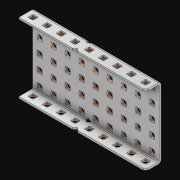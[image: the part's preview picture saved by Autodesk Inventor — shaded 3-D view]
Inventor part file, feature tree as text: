
AUTODESK INVENTOR PART (.ipt)
format: ipt  version: 2021 (Build 250183000, 183)  size: 3,008,512 bytes
history: native  units: in
note: dims shown in document units (in); Inventor stores cm internally (conversion verified against a paired STEP export)
features: extrude x64, other x63, sketch x4, thicken_offset x3, pattern_linear x3, imported_body x1
ambient origin geometry x8: Origin, YZ Plane, XZ Plane, XY Plane, X Axis, Y Axis, Z Axis, Center Point
bodies: Solid1 (feature_tree)
feature tree (138):
  thicken_offset  "Thicken1"
  thicken_offset  "Thicken2"
  thicken_offset  "Thicken3"
  pattern_linear  "Rectangular Pattern1"  Spacing1=0.001in  [1 undecoded]
  pattern_linear  "Rectangular Pattern2"  Spacing1=0.001in  [1 undecoded]
  pattern_linear  "Rectangular Pattern3"  Spacing1=0.182in  [1 undecoded]
  extrude  "Extrusion1"  Depth=0.063in TaperAngle=0.0deg
  sketch  "Sketch1"  dims[d0=0.001in]
  other  "Srf1"
  sketch  "Sketch2"  dims[d1=0.001in]
  other  "Srf2"
  sketch  "Sketch3"  dims[d2=0.001in]
  other  "Srf3"
  other  "Srf4"
  other  "Srf5"
  other  "Srf6"
  other  "Srf7"
  other  "Srf8"
  other  "Srf9"
  other  "Srf10"
  other  "Srf11"
  other  "Srf38"
  other  "Srf39"
  other  "Srf40"
  other  "Srf41"
  other  "Srf42"
  other  "Srf43"
  other  "Srf44"
  other  "Srf45"
  other  "Srf72"
  other  "Srf73"
  other  "Srf74"
  other  "Srf75"
  other  "Srf76"
  other  "Srf77"
  other  "Srf78"
  other  "Srf79"
  other  "Srf106"
  other  "Srf107"
  other  "Srf108"
  other  "Srf109"
  other  "Srf110"
  other  "Srf111"
  other  "Srf112"
  other  "Srf113"
  other  "Srf114"
  other  "Srf141"
  other  "Srf142"
  other  "Srf143"
  other  "Srf144"
  other  "Srf145"
  other  "Srf146"
  other  "Srf147"
  other  "Srf148"
  other  "Srf149"
  other  "Srf176"
  other  "Srf177"
  other  "Srf178"
  other  "Srf179"
  other  "Srf180"
  other  "Srf181"
  other  "Srf182"
  other  "Srf183"
  other  "Srf184"
  other  "Srf211"
  other  "Srf212"
  other  "Srf213"
  other  "Srf214"
  other  "Srf215"
  other  "Srf216"
  other  "Srf217"
  other  "Srf218"
  other  "Srf219"
  sketch  "Sketch4"  dims[d3=0.001in d4=0.001in d5=0.001in d6=0.182in d7=0.063in d8=0.0in d9=0.182in d10=0.063in d11=0.0in d12=0.182in d13=0.063in d14=0.0in d17=0.5in d18=3.5433in d20=0.5in d21=3.5433in d23=0.5in d24=1.9685in d26=0.5in d27=13.0in d28=0.0in]
  imported_body  "Imported1"
  extrude  "ExtrusionSrf1"  Depth=0.063in
  extrude  "ExtrusionSrf2"  Depth=0.063in TaperAngle=0.0deg
  extrude  "ExtrusionSrf3"  Depth=0.063in
  extrude  "ExtrusionSrf4"  Depth=0.063in TaperAngle=0.0deg
  extrude  "ExtrusionSrf5"  Depth=0.063in
  extrude  "ExtrusionSrf6"  Depth=0.063in
  extrude  "ExtrusionSrf7"  Depth=0.063in
  extrude  "ExtrusionSrf8"  Depth=0.063in
  extrude  "ExtrusionSrf9"  Depth=0.063in
  extrude  "ExtrusionSrf10"  Depth=0.063in
  extrude  "ExtrusionSrf11"  Depth=0.063in
  extrude  "ExtrusionSrf38"  TaperAngle=0.0deg  [1 undecoded]
  extrude  "ExtrusionSrf39"  [1 undecoded]
  extrude  "ExtrusionSrf40"  [1 undecoded]
  extrude  "ExtrusionSrf41"  [1 undecoded]
  extrude  "ExtrusionSrf42"  [1 undecoded]
  extrude  "ExtrusionSrf43"  [1 undecoded]
  extrude  "ExtrusionSrf44"  [1 undecoded]
  extrude  "ExtrusionSrf45"  [1 undecoded]
  extrude  "ExtrusionSrf72"  [1 undecoded]
  extrude  "ExtrusionSrf73"  [1 undecoded]
  extrude  "ExtrusionSrf74"  [1 undecoded]
  extrude  "ExtrusionSrf75"  [1 undecoded]
  extrude  "ExtrusionSrf76"  [1 undecoded]
  extrude  "ExtrusionSrf77"  [1 undecoded]
  extrude  "ExtrusionSrf78"  [1 undecoded]
  extrude  "ExtrusionSrf79"  [1 undecoded]
  extrude  "ExtrusionSrf106"  [1 undecoded]
  extrude  "ExtrusionSrf107"  [1 undecoded]
  extrude  "ExtrusionSrf108"  [1 undecoded]
  extrude  "ExtrusionSrf109"  [1 undecoded]
  extrude  "ExtrusionSrf110"  [1 undecoded]
  extrude  "ExtrusionSrf111"  [1 undecoded]
  extrude  "ExtrusionSrf112"  [1 undecoded]
  extrude  "ExtrusionSrf113"  [1 undecoded]
  extrude  "ExtrusionSrf114"  [1 undecoded]
  extrude  "ExtrusionSrf141"  [1 undecoded]
  extrude  "ExtrusionSrf142"  [1 undecoded]
  extrude  "ExtrusionSrf143"  [1 undecoded]
  extrude  "ExtrusionSrf144"  [1 undecoded]
  extrude  "ExtrusionSrf145"  [1 undecoded]
  extrude  "ExtrusionSrf146"  [1 undecoded]
  extrude  "ExtrusionSrf147"  [1 undecoded]
  extrude  "ExtrusionSrf148"  [1 undecoded]
  extrude  "ExtrusionSrf149"  [1 undecoded]
  extrude  "ExtrusionSrf176"  [1 undecoded]
  extrude  "ExtrusionSrf177"  [1 undecoded]
  extrude  "ExtrusionSrf178"  [1 undecoded]
  extrude  "ExtrusionSrf179"  [1 undecoded]
  extrude  "ExtrusionSrf180"  [1 undecoded]
  extrude  "ExtrusionSrf181"  [1 undecoded]
  extrude  "ExtrusionSrf182"  [1 undecoded]
  extrude  "ExtrusionSrf183"  [1 undecoded]
  extrude  "ExtrusionSrf184"  [1 undecoded]
  extrude  "ExtrusionSrf211"  [1 undecoded]
  extrude  "ExtrusionSrf212"  [1 undecoded]
  extrude  "ExtrusionSrf213"  [1 undecoded]
  extrude  "ExtrusionSrf214"  [1 undecoded]
  extrude  "ExtrusionSrf215"  [1 undecoded]
  extrude  "ExtrusionSrf216"  [1 undecoded]
  extrude  "ExtrusionSrf217"  [1 undecoded]
  extrude  "ExtrusionSrf218"  [1 undecoded]
  extrude  "ExtrusionSrf219"  [1 undecoded]
note: 55 required parameter values undecoded (feature->parameter linkage not recoverable at this tier; creation-order binding heuristic only, values carry confidence <= 0.55)
